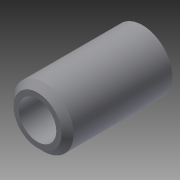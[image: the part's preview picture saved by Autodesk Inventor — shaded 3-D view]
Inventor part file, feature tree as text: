
AUTODESK INVENTOR PART (.ipt)
format: ipt  version: 2015 SP1 (Build 190203100, 203)  size: 87,040 bytes
history: native  units: in
note: dims shown in document units (in); Inventor stores cm internally (conversion verified against a paired STEP export)
features: extrude x1, chamfer x1, sketch x1
ambient origin geometry x8: Origin, YZ Plane, XZ Plane, XY Plane, X Axis, Y Axis, Z Axis, Center Point
bodies: Solid1 (feature_tree)
feature tree (3):
  extrude  "Extrusion1"  Depth=1.75in
  chamfer  "Chamfer1"  Distance=1.75in
  sketch  "Sketch1"  dims[d0=1.0in d2=0.625in d3=1.75in d4=0.0in d5=0.1in d6=0.125in d7=45.0deg]
